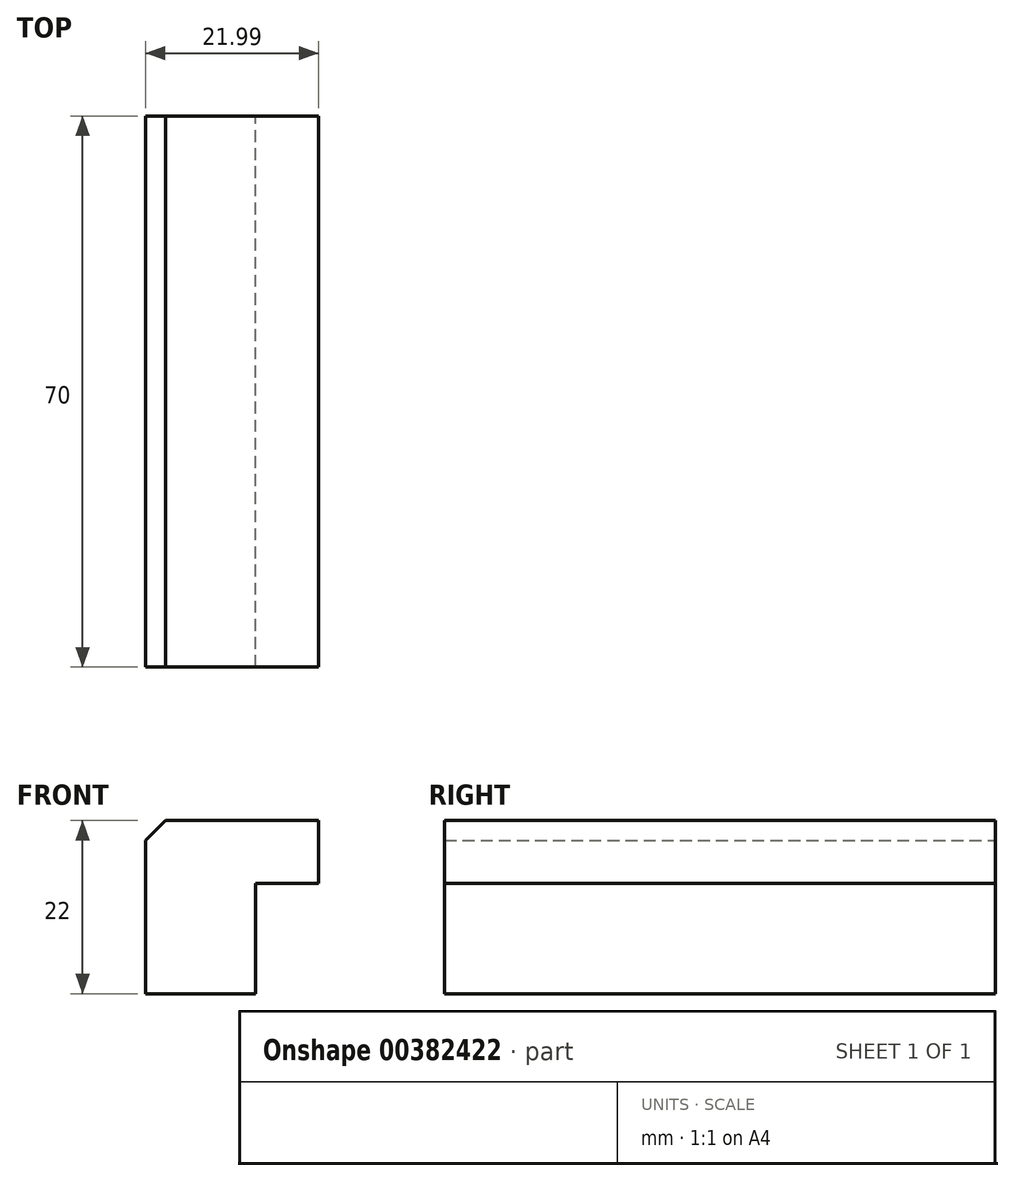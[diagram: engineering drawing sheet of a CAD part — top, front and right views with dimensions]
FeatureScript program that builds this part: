
annotation { "Feature Type Name" : "Feature", "Feature Type Description" : "" }
export const myFeature = defineFeature(function(context is Context, id is Id, definition is map)
    precondition{}
    {
        {
            var Q0;
            Q0=qCreatedBy(makeId("Front.planeOp"),FACE);
            var sketch = newSketch(context, id + "F0", { "sketchPlane" : qUnion([Q0])});
            skLineSegment(sketch, "E0", {"start": v(-19.73, 22) * mm, "end": v(-19.73, 0) * mm});
            skLineSegment(sketch, "E1", {"start": v(-19.73, 0) * mm, "end": v(-5.74, 0) * mm});
            skLineSegment(sketch, "E2", {"start": v(-5.74, 0) * mm, "end": v(-5.74, 14) * mm});
            skLineSegment(sketch, "E3", {"start": v(-5.74, 14) * mm, "end": v(2.26, 14) * mm});
            skLineSegment(sketch, "E4", {"start": v(2.26, 14) * mm, "end": v(2.26, 22) * mm});
            skLineSegment(sketch, "E5", {"start": v(2.26, 22) * mm, "end": v(-19.73, 22) * mm});
            skSolve(sketch);
        }
        {
            var Q0;
            Q0=qSketchRegion(id+"F0",true);
            extrude(context, id + "F1", {"entities" : qUnion([Q0]), "depth" : 70 * mm});
        }
        {
            var Q0;
            Q0=makeQuery(id+"F1.opExtrude","SWEPT_EDGE",EDGE,{"disambiguationData":[OSD([sQuery(id+"F0.wireOp",EDGE,"E0"),sQuery(id+"F0.wireOp",EDGE,"E5")])]});
            chamfer(context, id + "F2", {"entities" : qUnion([Q0]), "width" : 2.54 * mm, "tangentPropagation" : true});
        }
    });
